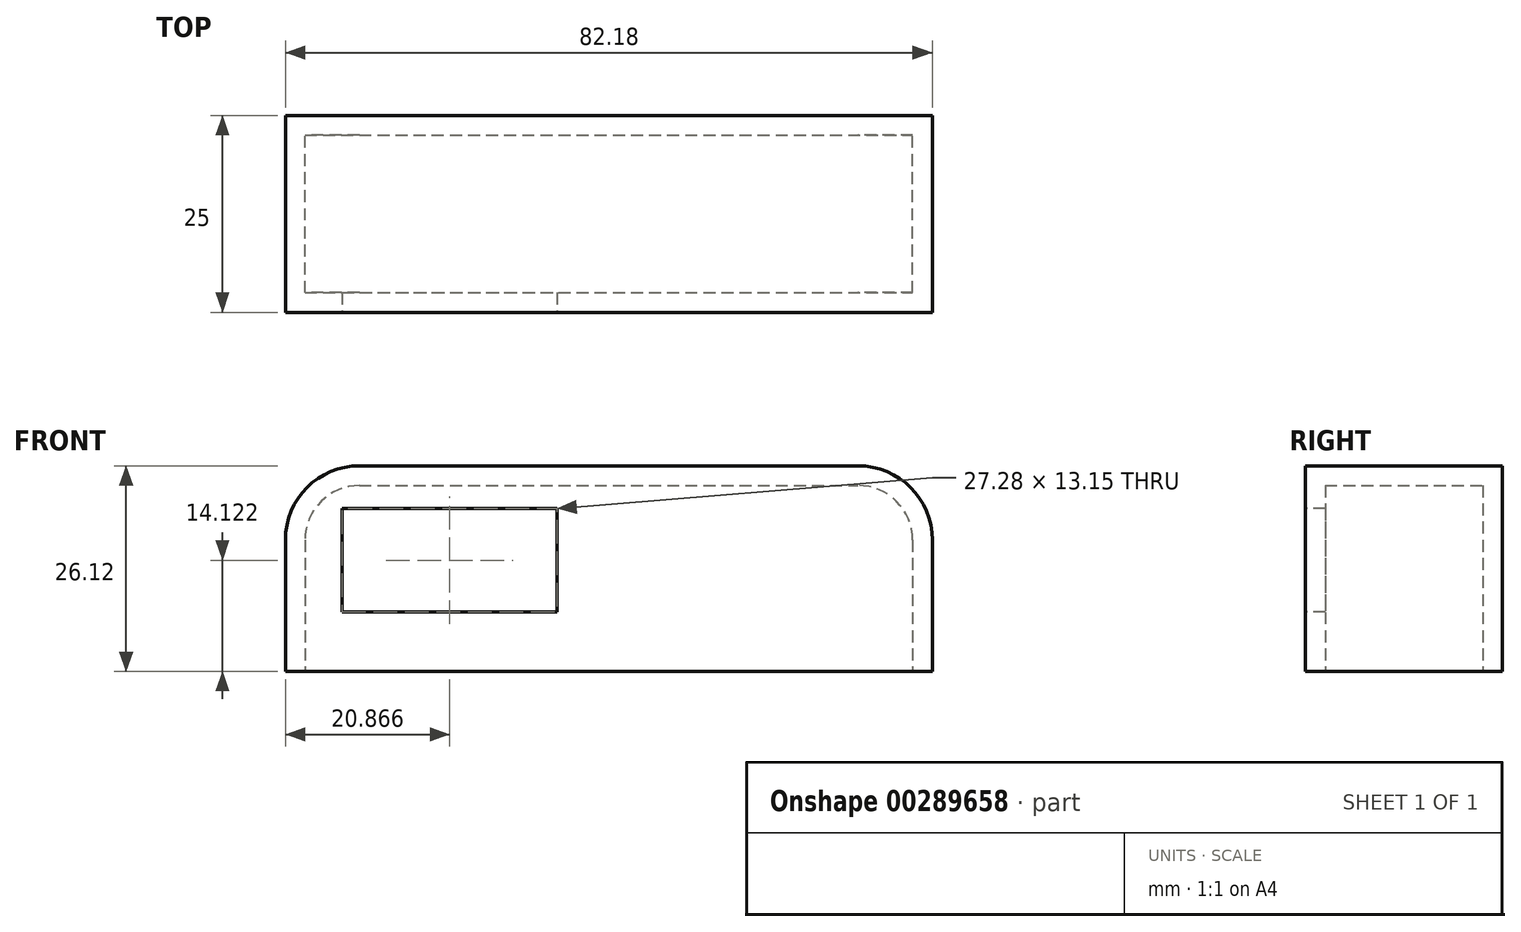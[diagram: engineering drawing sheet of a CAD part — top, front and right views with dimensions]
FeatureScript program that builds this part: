
annotation { "Feature Type Name" : "Feature", "Feature Type Description" : "" }
export const myFeature = defineFeature(function(context is Context, id is Id, definition is map)
    precondition{}
    {
        {
            var Q0;
            Q0=qCreatedBy(makeId("Front.planeOp"),FACE);
            var sketch = newSketch(context, id + "F0", { "sketchPlane" : qUnion([Q0])});
            skLineSegment(sketch, "E0.bottom", {"start": v(-30.4, 33.15) * mm, "end": v(51.77, 33.15) * mm});
            skLineSegment(sketch, "E0.top", {"start": v(-30.4, 7.03) * mm, "end": v(51.77, 7.03) * mm});
            skLineSegment(sketch, "E0.left", {"start": v(-30.4, 33.15) * mm, "end": v(-30.4, 7.03) * mm});
            skLineSegment(sketch, "E0.right", {"start": v(51.77, 33.15) * mm, "end": v(51.77, 7.03) * mm});
            skSolve(sketch);
        }
        {
            var Q0;
            Q0=makeQuery(id+"F0.imprint","IMPRINT",FACE,{"disambiguationData":[TD([[makeQuery(id+"F0.imprint","IMPRINT",EDGE,{"derivedFrom":sQuery(id+"F0.wireOp",EDGE,"E0.bottom")}),-1.0]])]});
            extrude(context, id + "F1", {"entities" : qUnion([Q0]), "depth" : 25 * mm});
        }
        {
            var Q0;
            Q0=makeQuery(id+"F1.opExtrude","SWEPT_EDGE",EDGE,{"disambiguationData":[OSD([sQuery(id+"F0.wireOp",EDGE,"E0.bottom"),sQuery(id+"F0.wireOp",EDGE,"E0.left")])]});
            var Q1;
            Q1=makeQuery(id+"F1.opExtrude","SWEPT_EDGE",EDGE,{"disambiguationData":[OSD([sQuery(id+"F0.wireOp",EDGE,"E0.bottom"),sQuery(id+"F0.wireOp",EDGE,"E0.right")])]});
            fillet(context, id + "F2", {"entities" : qUnion([Q0, Q1]), "radius" : 9.42 * mm, "tangentPropagation" : true, "allowEdgeOverflow" : false});
        }
        {
            var Q0;
            Q0=makeQuery(id+"F1.opExtrude","SWEPT_FACE",FACE,{"disambiguationData":[OSD([sQuery(id+"F0.wireOp",EDGE,"E0.top")])]});
            shell(context, id + "F3", {"entities" : qUnion([Q0]), "thickness" : 2.5 * mm});
        }
        {
            var Q0;
            Q0=makeQuery(id+"F1.opExtrude","CAP_FACE",FACE,{"disambiguationData":[OSD([sQuery(id+"F0.wireOp",EDGE,"E0.bottom"),sQuery(id+"F0.wireOp",EDGE,"E0.top"),sQuery(id+"F0.wireOp",EDGE,"E0.left"),sQuery(id+"F0.wireOp",EDGE,"E0.right")])],"isStart":false});
            var sketch = newSketch(context, id + "F4", { "sketchPlane" : qUnion([Q0])});
            skLineSegment(sketch, "E1.bottom", {"start": v(-23.18, 27.73) * mm, "end": v(4.1, 27.73) * mm});
            skLineSegment(sketch, "E1.top", {"start": v(-23.18, 14.58) * mm, "end": v(4.1, 14.58) * mm});
            skLineSegment(sketch, "E1.left", {"start": v(-23.18, 27.73) * mm, "end": v(-23.18, 14.58) * mm});
            skLineSegment(sketch, "E1.right", {"start": v(4.1, 27.73) * mm, "end": v(4.1, 14.58) * mm});
            skSolve(sketch);
        }
        {
            var Q0;
            Q0=makeQuery(id+"F4.imprint","IMPRINT",FACE,{"disambiguationData":[TD([[makeQuery(id+"F4.imprint","IMPRINT",EDGE,{"derivedFrom":sQuery(id+"F4.wireOp",EDGE,"WKbSVPl1-7i83-aVoN-4zf2-CM9SzWwqjyhN.bottom")}),-1.0]])]});
            var Q1;
            Q1=makeQuery(id+"F4.imprint","IMPRINT",FACE,{"disambiguationData":[TD([[makeQuery(id+"F4.imprint","IMPRINT",EDGE,{"derivedFrom":sQuery(id+"F4.wireOp",EDGE,"E1.bottom")}),-1.0]])]});
            extrude(context, id + "F5", {"entities" : qUnion([Q0, Q1]), "operationType" : NewBodyOperationType.REMOVE, "oppositeDirection" : true, "depth" : 14.9 * mm});
        }
    });
